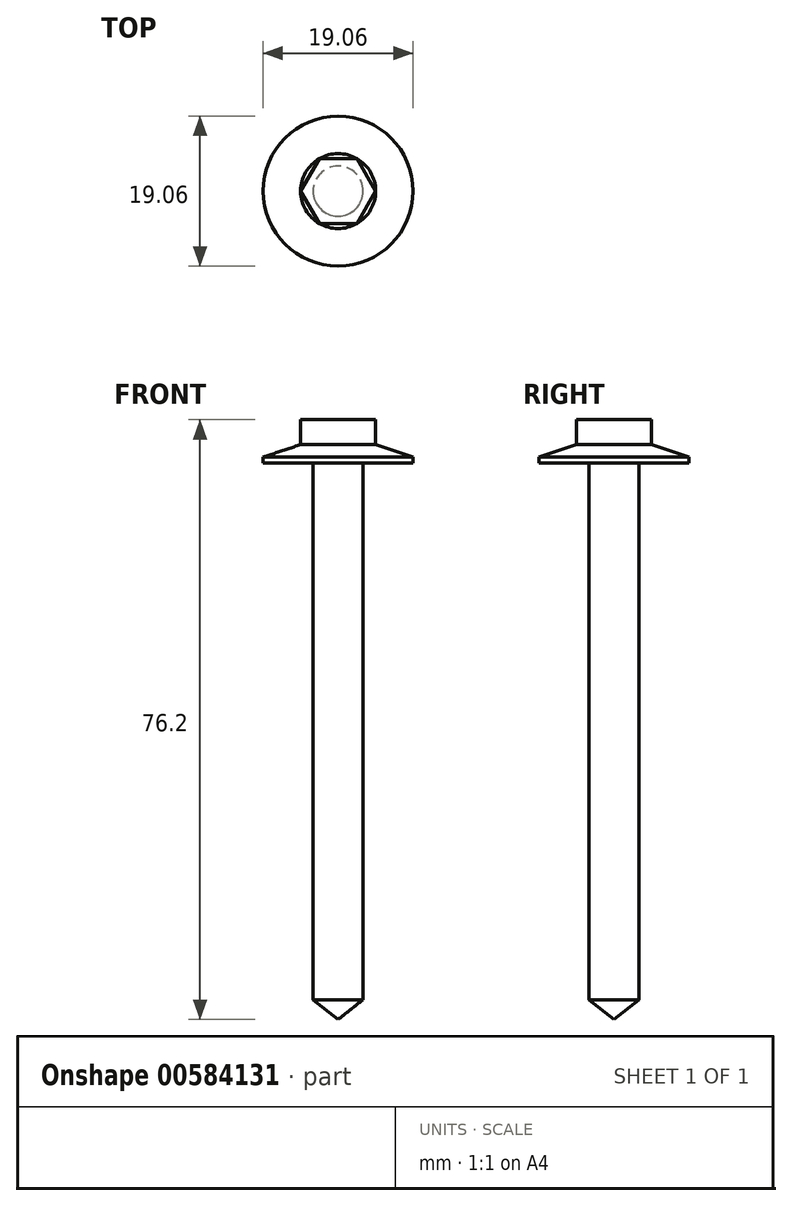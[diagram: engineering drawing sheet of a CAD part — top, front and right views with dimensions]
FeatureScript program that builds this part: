
annotation { "Feature Type Name" : "Feature", "Feature Type Description" : "" }
export const myFeature = defineFeature(function(context is Context, id is Id, definition is map)
    precondition{}
    {
        {
            var Q0;
            Q0=qCreatedBy(makeId("Front.planeOp"),FACE);
            var sketch = newSketch(context, id + "F0", { "sketchPlane" : qUnion([Q0])});
            skLineSegment(sketch, "E0", {"start": v(0, 0) * mm, "end": v(0, 76.2) * mm});
            skLineSegment(sketch, "E1", {"start": v(0, 76.2) * mm, "end": v(4.76, 76.2) * mm});
            skLineSegment(sketch, "E2", {"start": v(4.76, 76.2) * mm, "end": v(4.76, 73.03) * mm});
            skLineSegment(sketch, "E3", {"start": v(4.76, 73.02) * mm, "end": v(9.52, 71.44) * mm});
            skLineSegment(sketch, "E4", {"start": v(9.52, 71.44) * mm, "end": v(9.52, 70.68) * mm});
            skLineSegment(sketch, "E5", {"start": v(9.52, 70.68) * mm, "end": v(3.17, 70.68) * mm});
            skLineSegment(sketch, "E6", {"start": v(3.18, 70.68) * mm, "end": v(3.18, 2.51) * mm});
            skLineSegment(sketch, "E7", {"start": v(3.17, 2.51) * mm, "end": v(0, 0) * mm});
            skSolve(sketch);
        }
        {
            var Q0;
            Q0 = qSketchRegion(id + "F0", true);
            var Q1;
            Q1=sQuery(id+"F0.wireOp",EDGE,"E0");
            revolve(context, id + "F1", {"entities" : qUnion([Q0]), "axis" : qUnion([Q1]), "revolveType" : RevolveType.FULL});
        }
        {
            var Q0;
            Q0=makeQuery(id+"F1.opRevolve","SWEPT_FACE",FACE,{"disambiguationData":[OSD([sQuery(id+"F0.wireOp",EDGE,"E1")])]});
            var sketch = newSketch(context, id + "F2", { "sketchPlane" : qUnion([Q0])});
            skLineSegment(sketch, "E8", {"start": v(-2.38, 4.12) * mm, "end": v(2.38, 4.12) * mm});
            skLineSegment(sketch, "E9", {"start": v(2.38, 4.12) * mm, "end": v(4.76, 0) * mm});
            skLineSegment(sketch, "E10", {"start": v(4.76, 0) * mm, "end": v(2.38, -4.12) * mm});
            skLineSegment(sketch, "E11", {"start": v(2.38, -4.12) * mm, "end": v(-2.38, -4.12) * mm});
            skLineSegment(sketch, "E12", {"start": v(-2.38, -4.12) * mm, "end": v(-4.76, 0) * mm});
            skLineSegment(sketch, "E13", {"start": v(-4.76, 0) * mm, "end": v(-2.38, 4.12) * mm});
            skCircle(sketch, "E14", {"center": v(0, 0) * mm, "radius": 10.3 * mm});
            skSolve(sketch);
        }
        {
            var Q0;
            Q0 = qSketchRegion(id + "F2", true);
            extrude(context, id + "F3", {"entities" : qUnion([Q0]), "operationType" : NewBodyOperationType.REMOVE, "oppositeDirection" : true, "depth" : 1 / 203.2 * mm, "offsetDistance" : 25.4 * mm});
        }
    });
